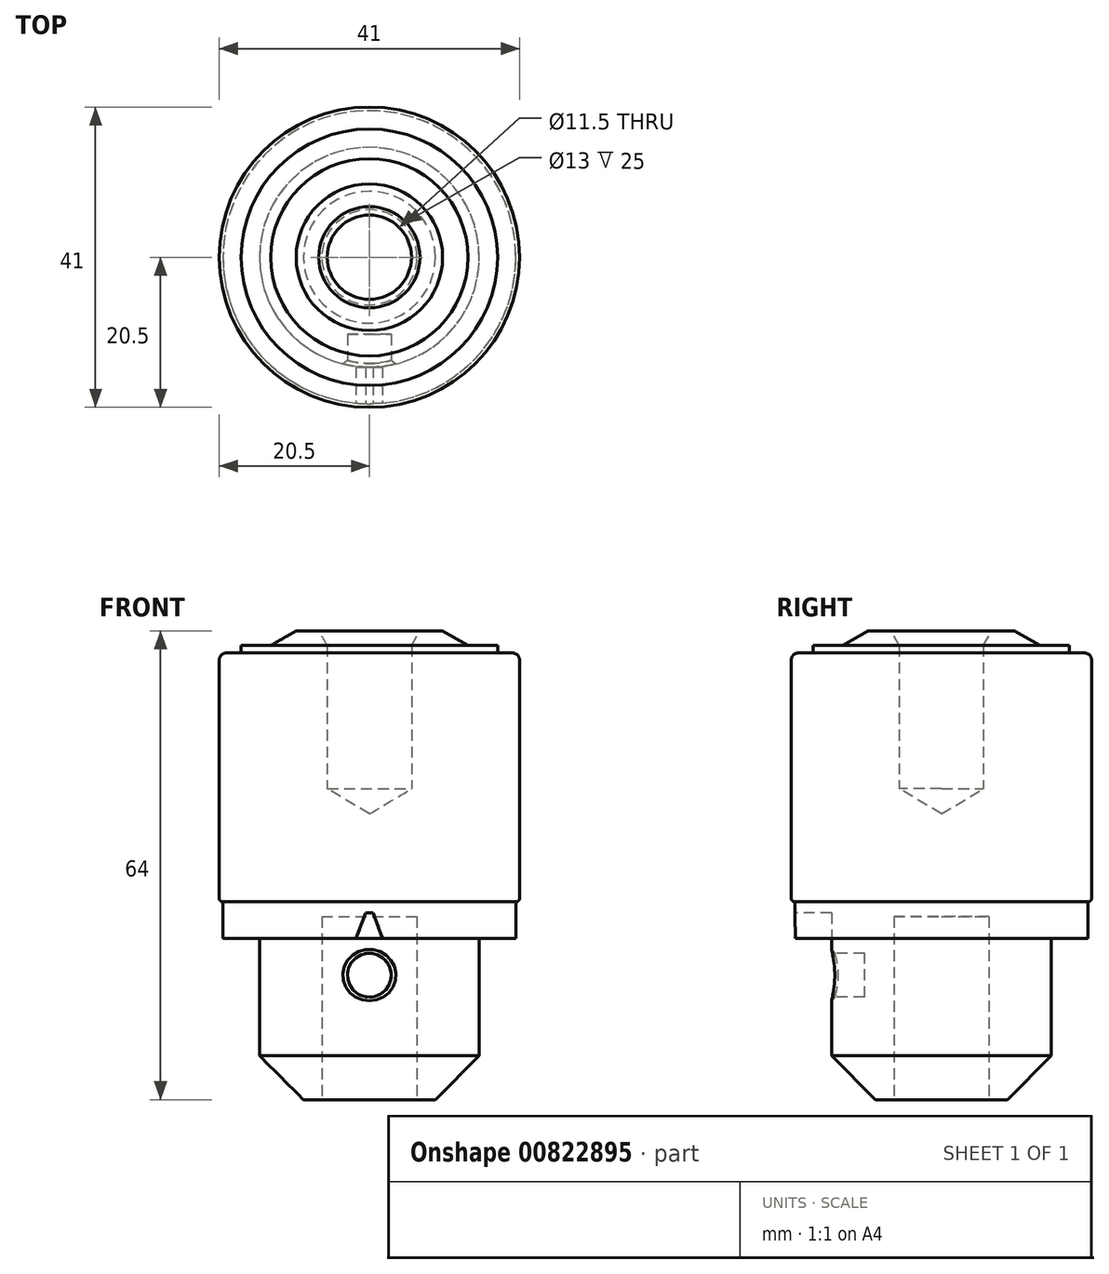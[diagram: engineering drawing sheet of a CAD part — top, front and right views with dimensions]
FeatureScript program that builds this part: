
annotation { "Feature Type Name" : "Feature", "Feature Type Description" : "" }
export const myFeature = defineFeature(function(context is Context, id is Id, definition is map)
    precondition{}
    {
        {
            var Q0;
            Q0=qCreatedBy(makeId("Front.planeOp"),FACE);
            var sketch = newSketch(context, id + "F0", { "sketchPlane" : qUnion([Q0])});
            skLineSegment(sketch, "E0", {"start": v(0, 0) * mm, "end": v(0, 65.5) * mm, "construction": true});
            skLineSegment(sketch, "E1", {"start": v(0, 34.99) * mm, "end": v(5.75, 38.44) * mm});
            skLineSegment(sketch, "E2", {"start": v(5.75, 38.44) * mm, "end": v(5.75, 57.99) * mm});
            skLineSegment(sketch, "E3", {"start": v(5.75, 57.99) * mm, "end": v(6.9, 59.99) * mm});
            skLineSegment(sketch, "E4", {"start": v(6.9, 59.99) * mm, "end": v(10, 59.99) * mm});
            skLineSegment(sketch, "E5", {"start": v(10, 59.99) * mm, "end": v(13.46, 57.99) * mm});
            skLineSegment(sketch, "E6", {"start": v(13.46, 57.99) * mm, "end": v(17.5, 57.99) * mm});
            skLineSegment(sketch, "E7", {"start": v(20.5, 56.99) * mm, "end": v(20.5, 22.99) * mm});
            skLineSegment(sketch, "E8", {"start": v(20, 17.99) * mm, "end": v(15, 17.99) * mm});
            skLineSegment(sketch, "E9", {"start": v(15, 17.99) * mm, "end": v(15, 1.99) * mm});
            skLineSegment(sketch, "E10", {"start": v(15, 1.99) * mm, "end": v(9, -4.01) * mm});
            skLineSegment(sketch, "E11", {"start": v(9, -4.01) * mm, "end": v(6.5, -4.01) * mm});
            skLineSegment(sketch, "E12", {"start": v(6.5, -4.01) * mm, "end": v(6.5, 20.99) * mm});
            skLineSegment(sketch, "E13", {"start": v(6.5, 20.99) * mm, "end": v(0, 20.99) * mm});
            skLineSegment(sketch, "E14", {"start": v(0, 20.99) * mm, "end": v(0, 34.99) * mm});
            skLineSegment(sketch, "E15", {"start": v(17.5, 57.99) * mm, "end": v(17.5, 56.99) * mm});
            skLineSegment(sketch, "E16", {"start": v(17.5, 56.99) * mm, "end": v(20.5, 56.99) * mm});
            skLineSegment(sketch, "E17", {"start": v(20, 17.99) * mm, "end": v(20, 22.99) * mm});
            skLineSegment(sketch, "E18", {"start": v(20, 22.99) * mm, "end": v(20.5, 22.99) * mm});
            skPoint(sketch, "E19.orphan", {"position": v(20.5, 17.99) * mm});
            skSolve(sketch);
        }
        {
            var Q0;
            Q0=makeQuery(id+"F0.imprint","IMPRINT",FACE,{"disambiguationData":[TD([[makeQuery(id+"F0.imprint","IMPRINT",EDGE,{"derivedFrom":sQuery(id+"F0.wireOp",EDGE,"E1")}),-1.0]])]});
            var Q1;
            Q1=sQuery(id+"F0.wireOp",EDGE,"E0");
            revolve(context, id + "F1", {"surfaceOperationType" : NewSurfaceOperationType.NEW, "entities" : qUnion([Q0]), "axis" : qUnion([Q1]), "revolveType" : RevolveType.FULL});
        }
        {
            var Q0;
            Q0=qCreatedBy(makeId("Front.planeOp"),FACE);
            cPlane(context, id + "F2", {"entities" : qUnion([Q0]), "cplaneType" : CPlaneType.OFFSET, "offset" : 20.5 * mm, "width" : 150 * mm, "height" : 150 * mm});
        }
        {
            var Q0;
            Q0=qCreatedBy(id+"F2.planeOp",FACE);
            var sketch = newSketch(context, id + "F3", { "sketchPlane" : qUnion([Q0])});
            skLineSegment(sketch, "E20.0", {"start": v(9, -4.01) * mm, "end": v(-9, -4.01) * mm, "construction": true});
            skLineSegment(sketch, "E21", {"start": v(0, -4.01) * mm, "end": v(0, 12.99) * mm, "construction": true});
            skCircle(sketch, "E22", {"center": v(0, 12.99) * mm, "radius": 3 * mm});
            skSolve(sketch);
        }
        {
            var Q0;
            Q0 = qSketchRegion(id + "F3", true);
            extrude(context, id + "F4", {"entities" : qUnion([Q0]), "operationType" : NewBodyOperationType.REMOVE, "oppositeDirection" : true, "depth" : 10 * mm, "offsetDistance" : 25 * mm});
        }
        {
            var Q0;
            Q0=makeQuery(id+"F4.boolean.opBoolean","INTERSECT",EDGE,{"derivedFrom":[makeQuery(id+"F1.opRevolve","SWEPT_FACE",FACE,{"disambiguationData":[OSD([sQuery(id+"F0.wireOp",EDGE,"E9")])]}),makeQuery(id+"F4.opExtrude","SWEPT_FACE",FACE,{"disambiguationData":[OSD([sQuery(id+"F3.wireOp",EDGE,"E22")])]})]});
            chamfer(context, id + "F5", {"entities" : qUnion([Q0]), "width" : 0.5 * mm, "tangentPropagation" : true});
        }
        {
            var Q0;
            Q0=makeQuery(id+"F1.opRevolve","SWEPT_EDGE",EDGE,{"disambiguationData":[OSD([sQuery(id+"F0.wireOp",EDGE,"E7"),sQuery(id+"F0.wireOp",EDGE,"E16")])]});
            fillet(context, id + "F6", {"entities" : qUnion([Q0]), "radius" : 1 * mm, "tangentPropagation" : true, "allowEdgeOverflow" : false});
        }
        {
            var Q0;
            Q0=makeQuery(id+"F1.opRevolve","SWEPT_EDGE",EDGE,{"disambiguationData":[OSD([sQuery(id+"F0.wireOp",EDGE,"E7"),sQuery(id+"F0.wireOp",EDGE,"E18")])]});
            fillet(context, id + "F7", {"entities" : qUnion([Q0]), "radius" : 0.5 * mm, "tangentPropagation" : true, "allowEdgeOverflow" : false});
        }
        {
            var Q0;
            Q0=qCreatedBy(id+"F2.planeOp",FACE);
            var sketch = newSketch(context, id + "F8", { "sketchPlane" : qUnion([Q0])});
            skLineSegment(sketch, "E23", {"start": v(-20, 17.99) * mm, "end": v(-20, 22.99) * mm, "construction": true});
            skLineSegment(sketch, "E24", {"start": v(20, 22.99) * mm, "end": v(20, 17.99) * mm, "construction": true});
            skLineSegment(sketch, "E25", {"start": v(-20, 20.49) * mm, "end": v(20, 20.49) * mm, "construction": true});
            skLineSegment(sketch, "E26", {"start": v(20, 20.49) * mm, "end": v(0, 30.44) * mm, "construction": true});
            skLineSegment(sketch, "E27", {"start": v(0, 30.44) * mm, "end": v(0, 20.49) * mm, "construction": true});
            skLineSegment(sketch, "E28.0", {"start": v(-0.5, 21.49) * mm, "end": v(0.5, 21.49) * mm});
            skLineSegment(sketch, "E29", {"start": v(0.5, 21.49) * mm, "end": v(2, 17.49) * mm});
            skLineSegment(sketch, "E30", {"start": v(2, 17.49) * mm, "end": v(0, 17.49) * mm});
            skLineSegment(sketch, "E31.MirrorCS", {"start": v(-0.5, 21.49) * mm, "end": v(-2, 17.49) * mm});
            skLineSegment(sketch, "E32.MirrorCS", {"start": v(-2, 17.49) * mm, "end": v(0, 17.49) * mm});
            skSolve(sketch);
        }
        {
            var Q0;
            Q0 = qSketchRegion(id + "F8", true);
            extrude(context, id + "F9", {"entities" : qUnion([Q0]), "operationType" : NewBodyOperationType.REMOVE, "oppositeDirection" : true, "depth" : 5.5 * mm, "offsetDistance" : 25 * mm});
        }
    });
